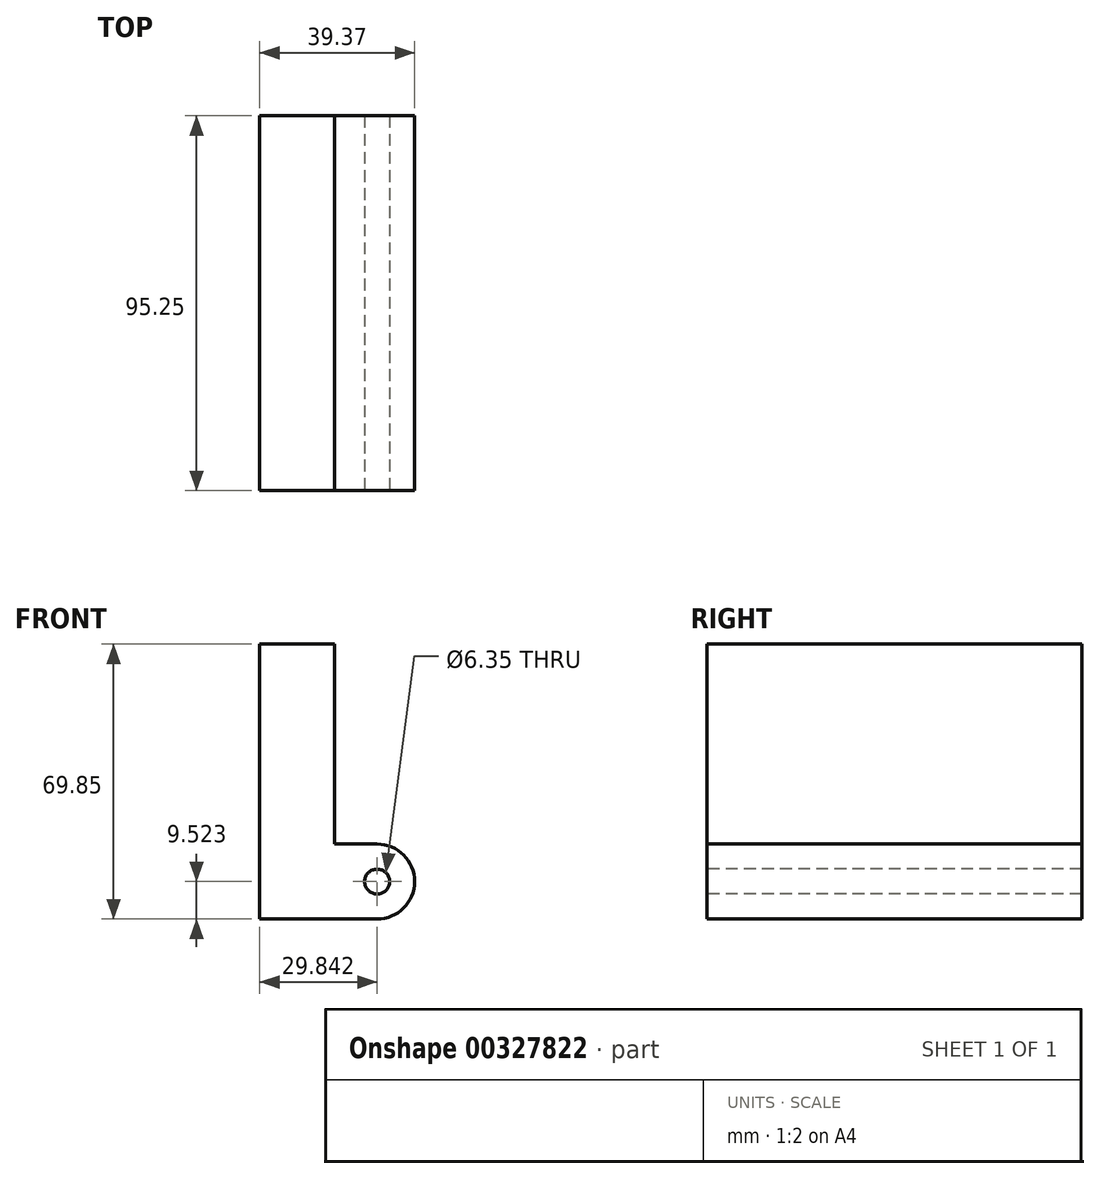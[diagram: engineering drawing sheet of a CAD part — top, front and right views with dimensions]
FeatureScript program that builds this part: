
annotation { "Feature Type Name" : "Feature", "Feature Type Description" : "" }
export const myFeature = defineFeature(function(context is Context, id is Id, definition is map)
    precondition{}
    {
        {
            var Q0;
            Q0=qCreatedBy(makeId("Front.planeOp"),FACE);
            var sketch = newSketch(context, id + "F0", { "sketchPlane" : qUnion([Q0])});
            skLineSegment(sketch, "E0", {"start": v(-31.52, 39.84) * mm, "end": v(-31.52, -30.01) * mm});
            skLineSegment(sketch, "E1", {"start": v(-31.52, -30.01) * mm, "end": v(7.85, -30.01) * mm});
            skLineSegment(sketch, "E2", {"start": v(7.85, -30.01) * mm, "end": v(7.85, -10.96) * mm});
            skLineSegment(sketch, "E3", {"start": v(7.85, -10.96) * mm, "end": v(-12.47, -10.96) * mm});
            skLineSegment(sketch, "E4", {"start": v(-12.47, -10.96) * mm, "end": v(-12.47, 39.84) * mm});
            skLineSegment(sketch, "E5", {"start": v(-12.47, 39.84) * mm, "end": v(-31.52, 39.84) * mm});
            skSolve(sketch);
        }
        {
            var Q0;
            Q0 = qSketchRegion(id + "F0", true);
            extrude(context, id + "F1", {"entities" : qUnion([Q0]), "depth" : 95.25 * mm});
        }
        {
            var Q0;
            Q0=makeQuery(id+"F1.opExtrude","SWEPT_EDGE",EDGE,{"disambiguationData":[OSD([sQuery(id+"F0.wireOp",EDGE,"ZwfVRYoF-0HMJ-9yn7-dHbi-jaOj4CS3ZJfg.right"),sQuery(id+"F0.wireOp",EDGE,"m2sn2Cli-I1w2-KdWA-kFbQ-TRgVPiavDf8P")])]});
            var Q1;
            Q1=makeQuery(id+"F1.opExtrude","SWEPT_EDGE",EDGE,{"disambiguationData":[OSD([sQuery(id+"F0.wireOp",EDGE,"ZwfVRYoF-0HMJ-9yn7-dHbi-jaOj4CS3ZJfg.top"),sQuery(id+"F0.wireOp",EDGE,"ZwfVRYoF-0HMJ-9yn7-dHbi-jaOj4CS3ZJfg.right")])]});
            var Q2;
            Q2=makeQuery(id+"F1.opExtrude","SWEPT_EDGE",EDGE,{"disambiguationData":[OSD([sQuery(id+"F0.wireOp",EDGE,"E2"),sQuery(id+"F0.wireOp",EDGE,"E3")])]});
            var Q3;
            Q3=makeQuery(id+"F1.opExtrude","SWEPT_EDGE",EDGE,{"disambiguationData":[OSD([sQuery(id+"F0.wireOp",EDGE,"E1"),sQuery(id+"F0.wireOp",EDGE,"E2")])]});
            fillet(context, id + "F2", {"entities" : qUnion([Q0, Q1, Q2, Q3]), "radius" : 9.52 * mm, "tangentPropagation" : true, "allowEdgeOverflow" : false});
        }
        {
            var Q0;
            Q0=makeQuery(id+"F1.opExtrude","CAP_FACE",FACE,{"disambiguationData":[OSD([sQuery(id+"F0.wireOp",EDGE,"E0"),sQuery(id+"F0.wireOp",EDGE,"E1"),sQuery(id+"F0.wireOp",EDGE,"E2"),sQuery(id+"F0.wireOp",EDGE,"E3"),sQuery(id+"F0.wireOp",EDGE,"E4"),sQuery(id+"F0.wireOp",EDGE,"E5")])],"isStart":false});
            var sketch = newSketch(context, id + "F3", { "sketchPlane" : qUnion([Q0])});
            skCircle(sketch, "E6", {"center": v(-1.68, -20.49) * mm, "radius": 3.18 * mm});
            skSolve(sketch);
        }
        {
            var Q0;
            Q0 = qSketchRegion(id + "F3", true);
            extrude(context, id + "F4", {"entities" : qUnion([Q0]), "operationType" : NewBodyOperationType.REMOVE, "endBound" : BoundingType.THROUGH_ALL, "oppositeDirection" : true, "depth" : 25.4 * mm});
        }
    });
